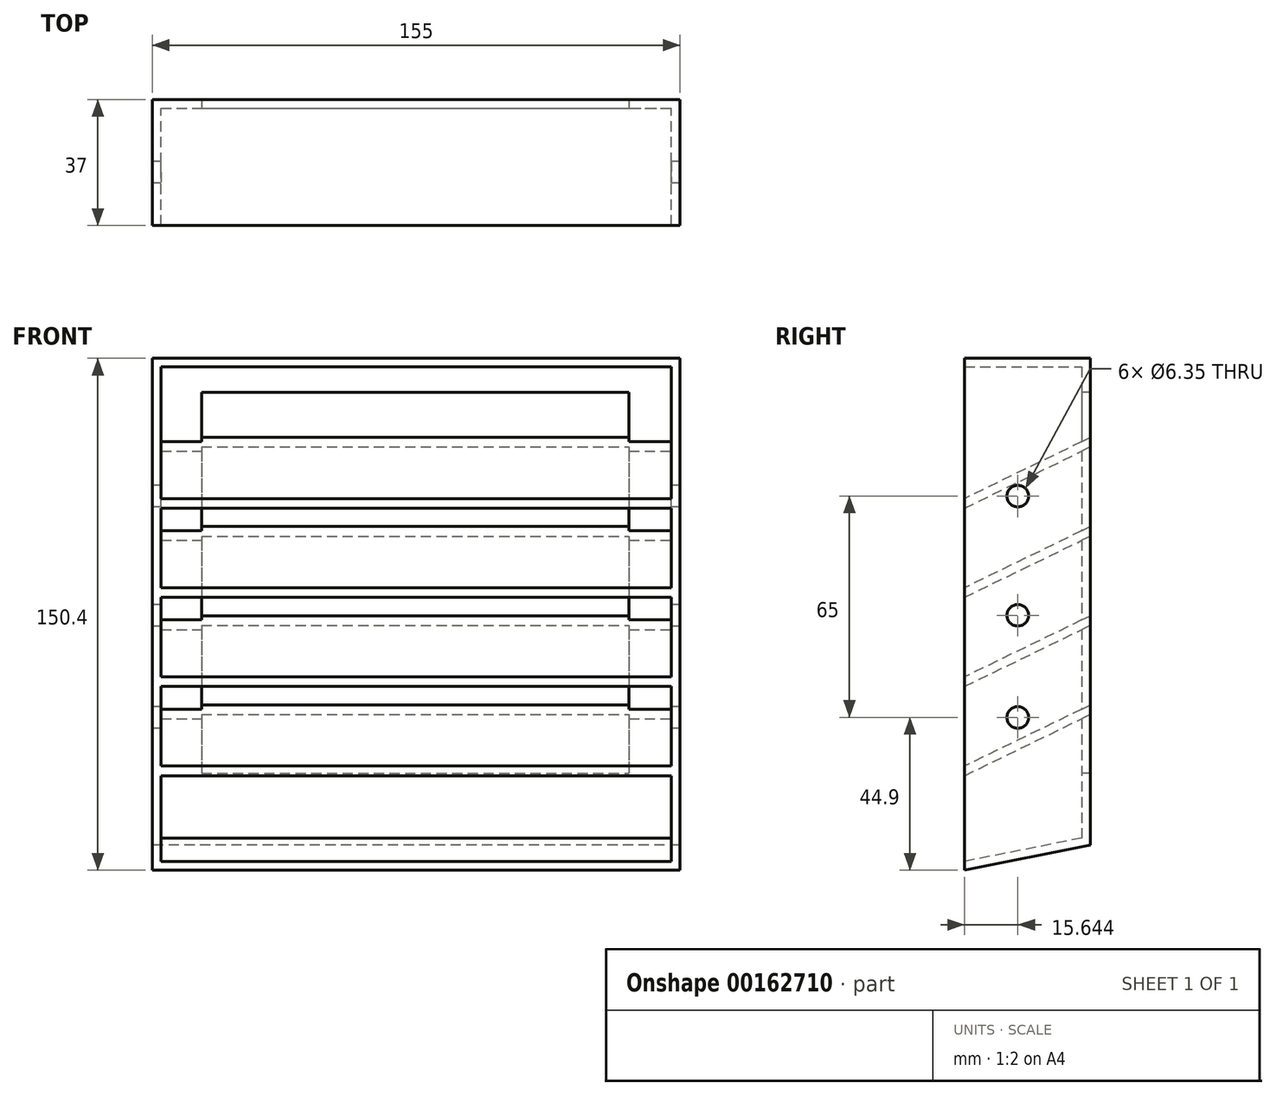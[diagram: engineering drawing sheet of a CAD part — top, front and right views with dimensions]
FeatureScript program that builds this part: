
annotation { "Feature Type Name" : "Feature", "Feature Type Description" : "" }
export const myFeature = defineFeature(function(context is Context, id is Id, definition is map)
    precondition{}
    {
        {
            var Q0;
            Q0=qCreatedBy(makeId("Front.planeOp"),FACE);
            var sketch = newSketch(context, id + "F0", { "sketchPlane" : qUnion([Q0])});
            skLineSegment(sketch, "E0.bottom", {"start": v(-77.5, 75.5) * mm, "end": v(77.5, 75.5) * mm});
            skLineSegment(sketch, "E0.top", {"start": v(-77.5, -75.5) * mm, "end": v(77.5, -75.5) * mm});
            skLineSegment(sketch, "E0.left", {"start": v(-77.5, 75.5) * mm, "end": v(-77.5, -75.5) * mm});
            skLineSegment(sketch, "E0.right", {"start": v(77.5, 75.5) * mm, "end": v(77.5, -75.5) * mm});
            skPoint(sketch, "E0.middle", {"position": v(0, 0) * mm});
            skPoint(sketch, "E1.visualSharp", {"position": v(77.5, 75.5) * mm});
            skPoint(sketch, "E2.visualSharp", {"position": v(77.5, -75.5) * mm});
            skSolve(sketch);
        }
        {
            var Q0;
            Q0=qSketchRegion(id+"F0",true);
            extrude(context, id + "F1", {"entities" : qUnion([Q0]), "depth" : 37 * mm});
        }
        {
            var Q0;
            Q0=makeQuery(id+"F1.opExtrude","CAP_EDGE",EDGE,{"disambiguationData":[OSD([sQuery(id+"F0.wireOp",EDGE,"E0.top")])],"isStart":true});
            chamfer(context, id + "F2", {"entities" : qUnion([Q0]), "chamferType" : ChamferType.TWO_OFFSETS, "width1" : 40 * mm, "oppositeDirection" : false, "width2" : 8 * mm});
        }
        {
            var Q0;
            Q0=makeQuery(id+"F1.opExtrude","CAP_FACE",FACE,{"disambiguationData":[OSD([sQuery(id+"F0.wireOp",EDGE,"E0.bottom"),sQuery(id+"F0.wireOp",EDGE,"E0.top"),sQuery(id+"F0.wireOp",EDGE,"E0.left"),sQuery(id+"F0.wireOp",EDGE,"E0.right"),sQuery(id+"F0.wireOp",EDGE,"E1.filletArc"),sQuery(id+"F0.wireOp",EDGE,"E2.filletArc")])],"isStart":false});
            shell(context, id + "F3", {"entities" : qUnion([Q0]), "thickness" : 2.54 * mm});
        }
        {
            var Q0;
            Q0=makeQuery(id+"F3.opShell","OFFSET_FACE",FACE,{"disambiguationData":[OSD([sQuery(id+"F0.wireOp",EDGE,"E0.bottom"),sQuery(id+"F0.wireOp",EDGE,"E0.top"),sQuery(id+"F0.wireOp",EDGE,"E0.left"),sQuery(id+"F0.wireOp",EDGE,"E0.right"),sQuery(id+"F0.wireOp",EDGE,"E1.filletArc"),sQuery(id+"F0.wireOp",EDGE,"E2.filletArc")])]});
            var sketch = newSketch(context, id + "F4", { "sketchPlane" : qUnion([Q0])});
            skPoint(sketch, "E3.middle", {"position": v(0, 0) * mm});
            skLineSegment(sketch, "E4.bottom", {"start": v(-63.05, 65.5) * mm, "end": v(62.5, 65.5) * mm});
            skLineSegment(sketch, "E4.top", {"start": v(-63.05, -46.42) * mm, "end": v(62.5, -46.42) * mm});
            skLineSegment(sketch, "E4.left", {"start": v(-63.05, 65.5) * mm, "end": v(-63.05, -46.42) * mm});
            skLineSegment(sketch, "E4.right", {"start": v(62.5, 65.5) * mm, "end": v(62.5, -46.42) * mm});
            skSolve(sketch);
        }
        {
            var Q0;
            Q0=makeQuery(id+"F4.imprint","IMPRINT",FACE,{"disambiguationData":[TD([[makeQuery(id+"F4.imprint","IMPRINT",EDGE,{"derivedFrom":sQuery(id+"F4.wireOp",EDGE,"E4.bottom")}),-1.0]])]});
            extrude(context, id + "F5", {"entities" : qUnion([Q0]), "operationType" : NewBodyOperationType.REMOVE, "oppositeDirection" : true, "depth" : 25.4 * mm});
        }
        {
            var Q0;
            Q0=makeQuery(id+"F1.opExtrude","SWEPT_FACE",FACE,{"disambiguationData":[OSD([sQuery(id+"F0.wireOp",EDGE,"E0.left")])]});
            var sketch = newSketch(context, id + "F6", { "sketchPlane" : qUnion([Q0])});
            skLineSegment(sketch, "E5.0.0", {"start": v(0, 75.5) * mm, "end": v(0, 75.5) * mm});
            skLineSegment(sketch, "E5.0.1", {"start": v(0, 75.5) * mm, "end": v(37, 75.5) * mm});
            skLineSegment(sketch, "E5.0.2", {"start": v(37, 75.5) * mm, "end": v(37, 75.5) * mm});
            skLineSegment(sketch, "E5.0.3", {"start": v(0, 75.5) * mm, "end": v(37, 75.5) * mm});
            skLineSegment(sketch, "E6.0.0", {"start": v(0, 75.5) * mm, "end": v(0, -67.5) * mm});
            skLineSegment(sketch, "E6.0.1", {"start": v(0, -67.5) * mm, "end": v(37, -74.9) * mm});
            skLineSegment(sketch, "E6.0.2", {"start": v(37, -74.9) * mm, "end": v(37, 75.5) * mm});
            skLineSegment(sketch, "E6.0.3", {"start": v(37, 75.5) * mm, "end": v(0, 75.5) * mm});
            skCircle(sketch, "E7", {"center": v(21.36, 0) * mm, "radius": 3.18 * mm});
            skCircle(sketch, "E8.0.1.0", {"center": v(21.36, -30) * mm, "radius": 3.18 * mm});
            skLineSegment(sketch, "E8.direction2", {"start": v(21.36, 0) * mm, "end": v(21.36, -30) * mm, "construction": true});
            skCircle(sketch, "E9", {"center": v(21.36, 35) * mm, "radius": 3.18 * mm});
            skSolve(sketch);
        }
        {
            var Q0;
            Q0=makeQuery(id+"F6.imprint","IMPRINT",FACE,{"disambiguationData":[TD([[makeQuery(id+"F6.imprint","IMPRINT",EDGE,{"derivedFrom":sQuery(id+"F6.wireOp",EDGE,"E7")}),1.0]])]});
            var Q1;
            Q1=makeQuery(id+"F6.imprint","IMPRINT",FACE,{"disambiguationData":[TD([[makeQuery(id+"F6.imprint","IMPRINT",EDGE,{"derivedFrom":sQuery(id+"F6.wireOp",EDGE,"E9")}),1.0]])]});
            var Q2;
            Q2=makeQuery(id+"F6.imprint","IMPRINT",FACE,{"disambiguationData":[TD([[makeQuery(id+"F6.imprint","IMPRINT",EDGE,{"derivedFrom":sQuery(id+"F6.wireOp",EDGE,"E8.0.1.0")}),1.0]])]});
            var Q3;
            Q3=sQuery(id+"F6.wireOp",EDGE,"E9");
            var Q4;
            Q4=sQuery(id+"F6.wireOp",EDGE,"E7");
            var Q5;
            Q5=sQuery(id+"F6.wireOp",EDGE,"E8.0.1.0");
            extrude(context, id + "F7", {"entities" : qUnion([Q0, Q1, Q2]), "operationType" : NewBodyOperationType.REMOVE, "surfaceEntities" : qUnion([Q3, Q4, Q5]), "endBound" : BoundingType.THROUGH_ALL, "oppositeDirection" : true, "depth" : 152.65 * mm});
        }
        {
            var Q0;
            Q0=makeQuery(id+"F3.opShell","OFFSET_FACE",FACE,{"disambiguationData":[OSD([sQuery(id+"F0.wireOp",EDGE,"E0.right")])]});
            var sketch = newSketch(context, id + "F8", { "sketchPlane" : qUnion([Q0])});
            skLineSegment(sketch, "E10", {"start": v(37, -47.1) * mm, "end": v(0, -29.15) * mm});
            skLineSegment(sketch, "E11", {"start": v(0, -29.15) * mm, "end": v(0, -26.33) * mm});
            skLineSegment(sketch, "E12", {"start": v(0, -26.33) * mm, "end": v(37, -44.28) * mm});
            skLineSegment(sketch, "E13", {"start": v(37, -44.28) * mm, "end": v(37, -47.1) * mm});
            skLineSegment(sketch, "E14", {"start": v(37, -20.91) * mm, "end": v(0, -2.96) * mm});
            skLineSegment(sketch, "E15", {"start": v(0, -2.96) * mm, "end": v(0, -0.14) * mm});
            skLineSegment(sketch, "E16", {"start": v(0, -0.14) * mm, "end": v(37, -18.1) * mm});
            skLineSegment(sketch, "E17", {"start": v(37, -18.1) * mm, "end": v(37, -20.91) * mm});
            skLineSegment(sketch, "E18", {"start": v(37, 5.28) * mm, "end": v(0, 23.23) * mm});
            skLineSegment(sketch, "E19", {"start": v(0, 23.23) * mm, "end": v(0, 26.05) * mm});
            skLineSegment(sketch, "E20", {"start": v(0, 26.05) * mm, "end": v(37, 8.1) * mm});
            skLineSegment(sketch, "E21", {"start": v(37, 8.1) * mm, "end": v(37, 5.28) * mm});
            skLineSegment(sketch, "E22", {"start": v(37, 31.47) * mm, "end": v(0, 49.42) * mm});
            skLineSegment(sketch, "E23", {"start": v(0, 49.42) * mm, "end": v(0, 52.25) * mm});
            skLineSegment(sketch, "E24", {"start": v(0, 52.25) * mm, "end": v(37, 34.3) * mm});
            skLineSegment(sketch, "E25", {"start": v(37, 34.3) * mm, "end": v(37, 31.47) * mm});
            skSolve(sketch);
        }
        {
            var Q0;
            Q0 = qSketchRegion(id + "F8", true);
            var Q1;
            Q1=makeQuery(id+"F1.opExtrude","SWEPT_FACE",FACE,{"disambiguationData":[OSD([sQuery(id+"F0.wireOp",EDGE,"E0.left")])]});
            var Q2;
            Q2=makeQuery(id+"F1.opExtrude","SWEPT_FACE",FACE,{"disambiguationData":[OSD([sQuery(id+"F0.wireOp",EDGE,"E0.left")])]});
            var Q3;
            Q3=makeQuery(id+"F1.opExtrude","SWEPT_BODY",BODY,{"disambiguationData":[OSD([sQuery(id+"F0.wireOp",EDGE,"E0.bottom"),sQuery(id+"F0.wireOp",EDGE,"E0.top"),sQuery(id+"F0.wireOp",EDGE,"E0.left"),sQuery(id+"F0.wireOp",EDGE,"E0.right")])]});
            extrude(context, id + "F9", {"entities" : qUnion([Q0]), "operationType" : NewBodyOperationType.ADD, "endBound" : BoundingType.UP_TO_SURFACE, "endBoundEntityFace" : qUnion([Q1]), "depth" : 142.24 * mm});
        }
    });
